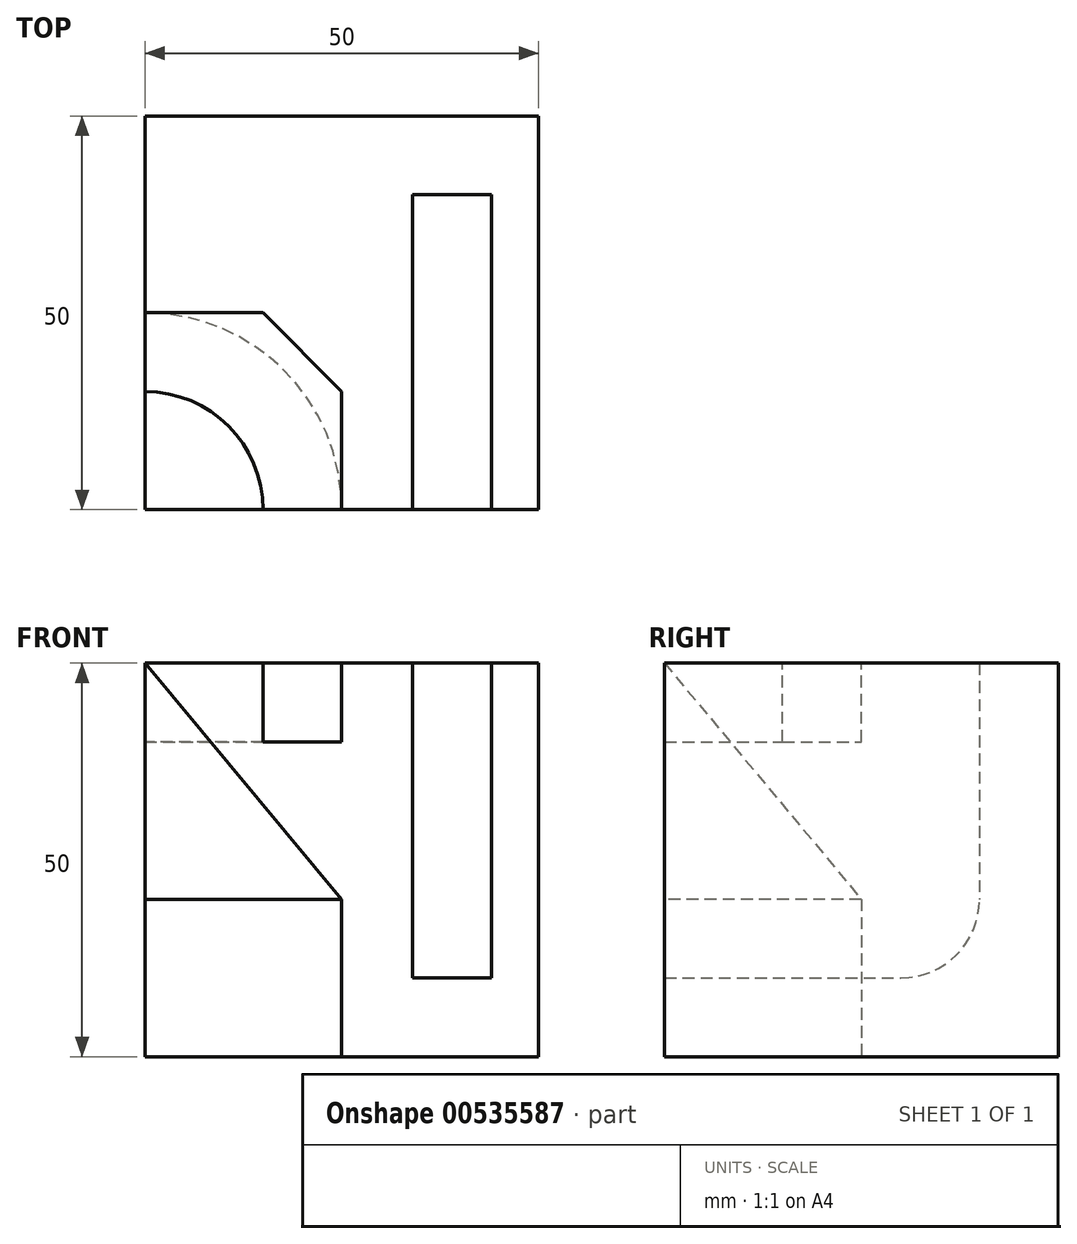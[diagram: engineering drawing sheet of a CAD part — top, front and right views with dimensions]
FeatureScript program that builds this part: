
annotation { "Feature Type Name" : "Feature", "Feature Type Description" : "" }
export const myFeature = defineFeature(function(context is Context, id is Id, definition is map)
    precondition{}
    {
        {
            var Q0;
            Q0=qCreatedBy(makeId("Top.planeOp"),FACE);
            var sketch = newSketch(context, id + "F0", { "sketchPlane" : qUnion([Q0])});
            skLineSegment(sketch, "E0.bottom", {"start": v(0, 0) * mm, "end": v(50, 0) * mm});
            skLineSegment(sketch, "E0.top", {"start": v(0, 50) * mm, "end": v(50, 50) * mm});
            skLineSegment(sketch, "E0.left", {"start": v(0, 0) * mm, "end": v(0, 50) * mm});
            skLineSegment(sketch, "E0.right", {"start": v(50, 0) * mm, "end": v(50, 50) * mm});
            skSolve(sketch);
        }
        {
            var Q0;
            Q0 = qSketchRegion(id + "F0", true);
            extrude(context, id + "F1", {"entities" : qUnion([Q0]), "depth" : 50 * mm, "offsetDistance" : 25 * mm});
        }
        {
            var Q0;
            Q0=makeQuery(id+"F1.opExtrude","CAP_FACE",FACE,{"disambiguationData":[OSD([sQuery(id+"F0.wireOp",EDGE,"E0.bottom"),sQuery(id+"F0.wireOp",EDGE,"E0.top"),sQuery(id+"F0.wireOp",EDGE,"E0.left"),sQuery(id+"F0.wireOp",EDGE,"E0.right")])],"isStart":false});
            var sketch = newSketch(context, id + "F2", { "sketchPlane" : qUnion([Q0])});
            skCircle(sketch, "E1", {"center": v(0, 0) * mm, "radius": 15 * mm});
            skLineSegment(sketch, "E2", {"start": v(0, 0) * mm, "end": v(25, 0) * mm});
            skLineSegment(sketch, "E3", {"start": v(0, 0) * mm, "end": v(0, 25) * mm});
            skLineSegment(sketch, "E4", {"start": v(0, 25) * mm, "end": v(15, 25) * mm});
            skLineSegment(sketch, "E5", {"start": v(25, 0) * mm, "end": v(25, 15) * mm});
            skLineSegment(sketch, "E6", {"start": v(15, 25) * mm, "end": v(25, 15) * mm});
            skLineSegment(sketch, "E7", {"start": v(0, 25) * mm, "end": v(0, 15) * mm});
            skLineSegment(sketch, "E8", {"start": v(15, 0) * mm, "end": v(25, 0) * mm});
            skSolve(sketch);
        }
        {
            var Q0;
            {var subQ0=sQuery(id+"F2.wireOp",EDGE,"E2");Q0=makeQuery(id+"F2.imprint","IMPRINT",FACE,{"disambiguationData":[TD([[makeQuery(id+"F2.imprint","IMPRINT",EDGE,{"derivedFrom":subQ0}),-1.0]])]});}
            var Q1;
            Q1=makeQuery(id+"F2.imprint","IMPRINT",FACE,{"disambiguationData":[TD([[makeQuery(id+"F2.imprint","IMPRINT",EDGE,{"derivedFrom":sQuery(id+"F2.wireOp",EDGE,"E4")}),-1.0]])]});
            extrude(context, id + "F3", {"entities" : qUnion([Q0, Q1]), "operationType" : NewBodyOperationType.REMOVE, "oppositeDirection" : true, "depth" : 10 * mm, "offsetDistance" : 25 * mm});
        }
        {
            var Q0;
            Q0=makeQuery(id+"F1.opExtrude","CAP_FACE",FACE,{"disambiguationData":[OSD([sQuery(id+"F0.wireOp",EDGE,"E0.bottom"),sQuery(id+"F0.wireOp",EDGE,"E0.top"),sQuery(id+"F0.wireOp",EDGE,"E0.left"),sQuery(id+"F0.wireOp",EDGE,"E0.right")])],"isStart":true});
            var sketch = newSketch(context, id + "F4", { "sketchPlane" : qUnion([Q0])});
            skLineSegment(sketch, "E9", {"start": v(0, 0) * mm, "end": v(25, 0) * mm});
            skLineSegment(sketch, "E10", {"start": v(0, 0) * mm, "end": v(0, -25) * mm});
            skCircle(sketch, "E11", {"center": v(0, 0) * mm, "radius": 25 * mm});
            skSolve(sketch);
        }
        {
            var Q0;
            Q0 = qSketchRegion(id + "F4", true);
            extrude(context, id + "F5", {"entities" : qUnion([Q0]), "operationType" : NewBodyOperationType.REMOVE, "oppositeDirection" : true, "depth" : 20 * mm, "offsetDistance" : 25 * mm});
        }
        {
            var Q0;
            Q0=makeQuery(id+"F1.opExtrude","SWEPT_FACE",FACE,{"disambiguationData":[OSD([sQuery(id+"F0.wireOp",EDGE,"E0.left")])]});
            var sketch = newSketch(context, id + "F6", { "sketchPlane" : qUnion([Q0])});
            skLineSegment(sketch, "E12", {"start": v(0, 50) * mm, "end": v(-25, 20) * mm});
            skSolve(sketch);
        }
        {
            var Q0;
            Q0=makeQuery(id+"F1.opExtrude","SWEPT_FACE",FACE,{"disambiguationData":[OSD([sQuery(id+"F0.wireOp",EDGE,"E0.bottom")])]});
            var sketch = newSketch(context, id + "F7", { "sketchPlane" : qUnion([Q0])});
            skLineSegment(sketch, "E13", {"start": v(0, 50) * mm, "end": v(25, 20) * mm});
            skSolve(sketch);
        }
        {
            var Q0;
            Q0=makeQuery(id+"F7.imprint","IMPRINT",FACE,{"disambiguationData":[TD([[makeQuery(id+"F7.imprint","IMPRINT",EDGE,{"derivedFrom":sQuery(id+"F7.wireOp",EDGE,"E13")}),-1.0]])]});
            var Q1;
            Q1=makeQuery(id+"F6.imprint","IMPRINT",FACE,{"disambiguationData":[TD([[makeQuery(id+"F6.imprint","IMPRINT",EDGE,{"derivedFrom":sQuery(id+"F6.wireOp",EDGE,"E12")}),1.0]])]});
            var Q2;
            Q2=makeQuery(id+"F1.opExtrude","SWEPT_EDGE",EDGE,{"disambiguationData":[OSD([sQuery(id+"F0.wireOp",EDGE,"E0.bottom"),sQuery(id+"F0.wireOp",EDGE,"E0.left")])]});
            revolve(context, id + "F8", {"operationType" : NewBodyOperationType.REMOVE, "entities" : qUnion([Q0, Q1]), "axis" : qUnion([Q2]), "revolveType" : RevolveType.FULL, "oppositeDirection" : true});
        }
        {
            var Q0;
            {var subQ0=sQuery(id+"F0.wireOp",EDGE,"E0.left");var subQ1=sQuery(id+"F0.wireOp",EDGE,"E0.top");var subQ2=sQuery(id+"F0.wireOp",EDGE,"E0.right");var subQ3=sQuery(id+"F0.wireOp",EDGE,"E0.bottom");Q0=makeQuery(id+"F3.boolean.opBoolean","SPLIT",FACE,{"disambiguationData":[TD([makeQuery(id+"F1.opExtrude","SWEPT_FACE",FACE,{"disambiguationData":[OSD([subQ1])]})])],"derivedFrom":makeQuery(id+"F1.opExtrude","CAP_FACE",FACE,{"disambiguationData":[OSD([subQ3,subQ1,subQ0,subQ2])],"isStart":false})});}
            var sketch = newSketch(context, id + "F9", { "sketchPlane" : qUnion([Q0])});
            skLineSegment(sketch, "E14", {"start": v(0, 0) * mm, "end": v(34, 0) * mm});
            skLineSegment(sketch, "E15", {"start": v(34, 0) * mm, "end": v(44, 0) * mm});
            skLineSegment(sketch, "E16", {"start": v(0, 50) * mm, "end": v(34, 50) * mm});
            skLineSegment(sketch, "E17", {"start": v(34, 50) * mm, "end": v(44, 50) * mm});
            skSolve(sketch);
        }
        {
            var Q0;
            Q0=qCreatedBy(makeId("Right.planeOp"),FACE);
            cPlane(context, id + "F10", {"entities" : qUnion([Q0]), "cplaneType" : CPlaneType.OFFSET, "offset" : 44 * mm, "width" : 150 * mm, "height" : 150 * mm});
        }
        {
            var Q0;
            Q0=qCreatedBy(id+"F10.planeOp",FACE);
            var sketch = newSketch(context, id + "F11", { "sketchPlane" : qUnion([Q0])});
            skLineSegment(sketch, "E18", {"start": v(0, 0) * mm, "end": v(0, 10) * mm});
            skLineSegment(sketch, "E19", {"start": v(50, 50) * mm, "end": v(40, 50) * mm});
            skLineSegment(sketch, "E20.top", {"start": v(30, 20) * mm, "end": v(40, 20) * mm});
            skLineSegment(sketch, "E20.left", {"start": v(30, 10) * mm, "end": v(30, 20) * mm});
            skLineSegment(sketch, "E21", {"start": v(0, 10) * mm, "end": v(0, 50) * mm});
            skLineSegment(sketch, "E22", {"start": v(40, 50) * mm, "end": v(0, 50) * mm});
            skLineSegment(sketch, "E23", {"start": v(0, 10) * mm, "end": v(30, 10) * mm});
            skLineSegment(sketch, "E24", {"start": v(40, 50) * mm, "end": v(40, 20) * mm});
            skArc(sketch, "E25", {"start": v(30, 10) * mm, "mid": v(37.07, 12.93) * mm, "end": v(40, 20) * mm});
            skSolve(sketch);
        }
        {
            var Q0;
            Q0 = qSketchRegion(id + "F11", true);
            extrude(context, id + "F12", {"entities" : qUnion([Q0]), "operationType" : NewBodyOperationType.REMOVE, "oppositeDirection" : true, "depth" : 10 * mm, "offsetDistance" : 25 * mm});
        }
    });
